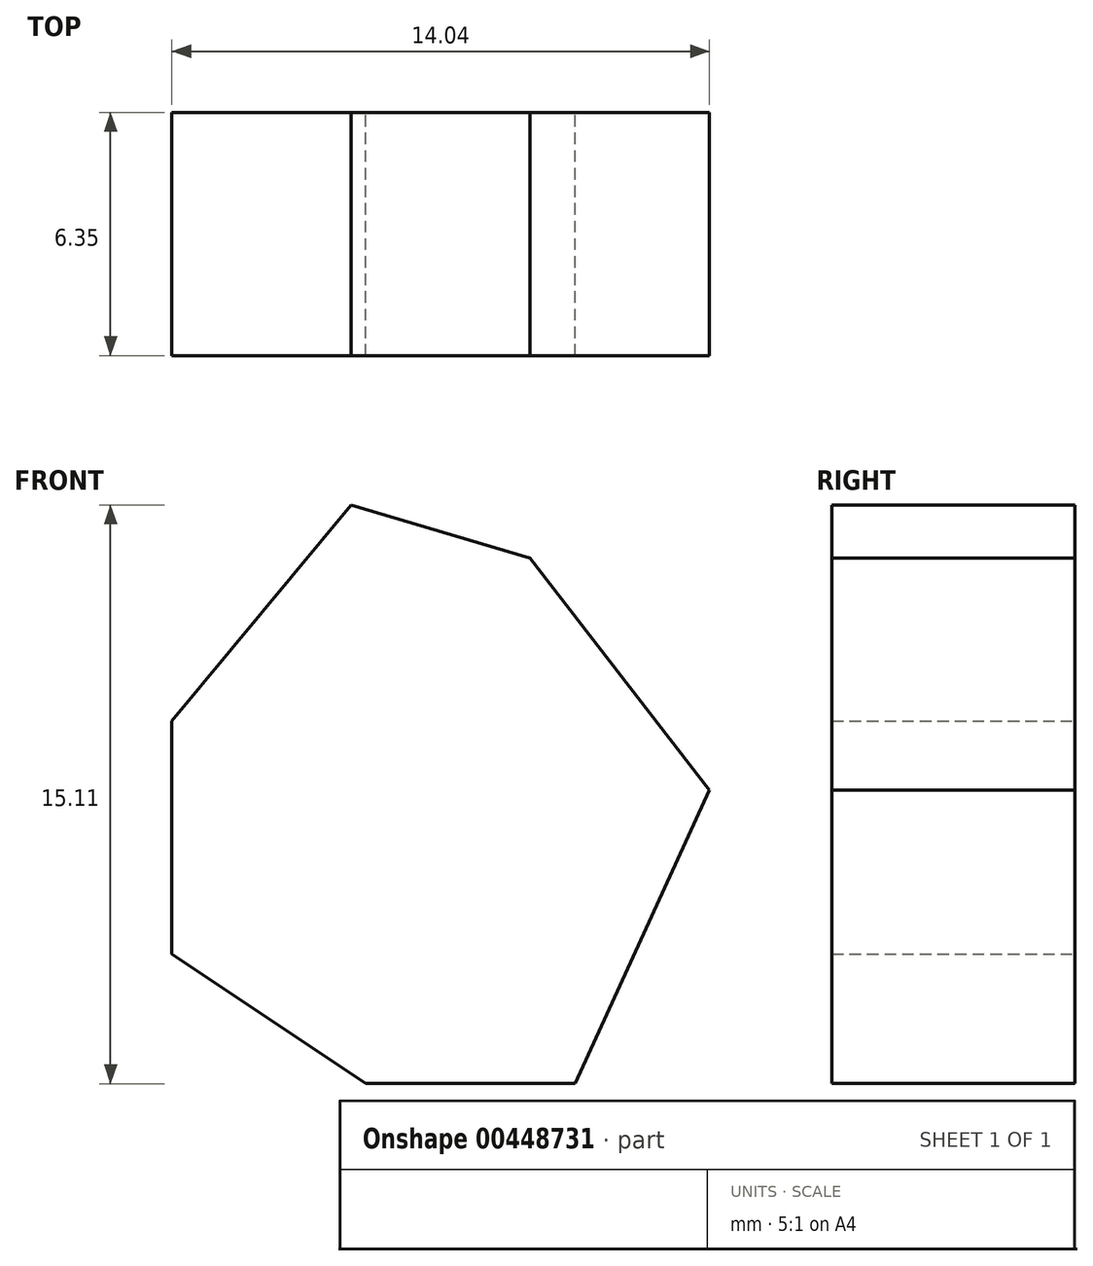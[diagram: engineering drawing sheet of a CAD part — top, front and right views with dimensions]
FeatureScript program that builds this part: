
annotation { "Feature Type Name" : "Feature", "Feature Type Description" : "" }
export const myFeature = defineFeature(function(context is Context, id is Id, definition is map)
    precondition{}
    {
        {
            var Q0;
            Q0=qCreatedBy(makeId("Front.planeOp"),FACE);
            var sketch = newSketch(context, id + "F0", { "sketchPlane" : qUnion([Q0])});
            skLineSegment(sketch, "E0", {"start": v(-108.02, 33.62) * mm, "end": v(-112.7, 27.97) * mm});
            skLineSegment(sketch, "E1", {"start": v(-112.7, 27.97) * mm, "end": v(-112.7, 21.9) * mm});
            skLineSegment(sketch, "E2", {"start": v(-112.7, 21.9) * mm, "end": v(-107.63, 18.51) * mm});
            skLineSegment(sketch, "E3", {"start": v(-107.63, 18.51) * mm, "end": v(-102.17, 18.51) * mm});
            skLineSegment(sketch, "E4", {"start": v(-102.17, 18.51) * mm, "end": v(-98.66, 26.18) * mm});
            skLineSegment(sketch, "E5", {"start": v(-98.66, 26.18) * mm, "end": v(-103.34, 32.24) * mm});
            skLineSegment(sketch, "E6", {"start": v(-103.34, 32.24) * mm, "end": v(-108.02, 33.62) * mm});
            skSolve(sketch);
        }
        {
            var Q0;
            Q0=makeQuery(id+"F0.imprint","IMPRINT",FACE,{"disambiguationData":[TD([[makeQuery(id+"F0.imprint","IMPRINT",EDGE,{"derivedFrom":sQuery(id+"F0.wireOp",EDGE,"E0")}),1.0]])]});
            extrude(context, id + "F1", {"entities" : qUnion([Q0]), "depth" : 6.35 * mm});
        }
    });
